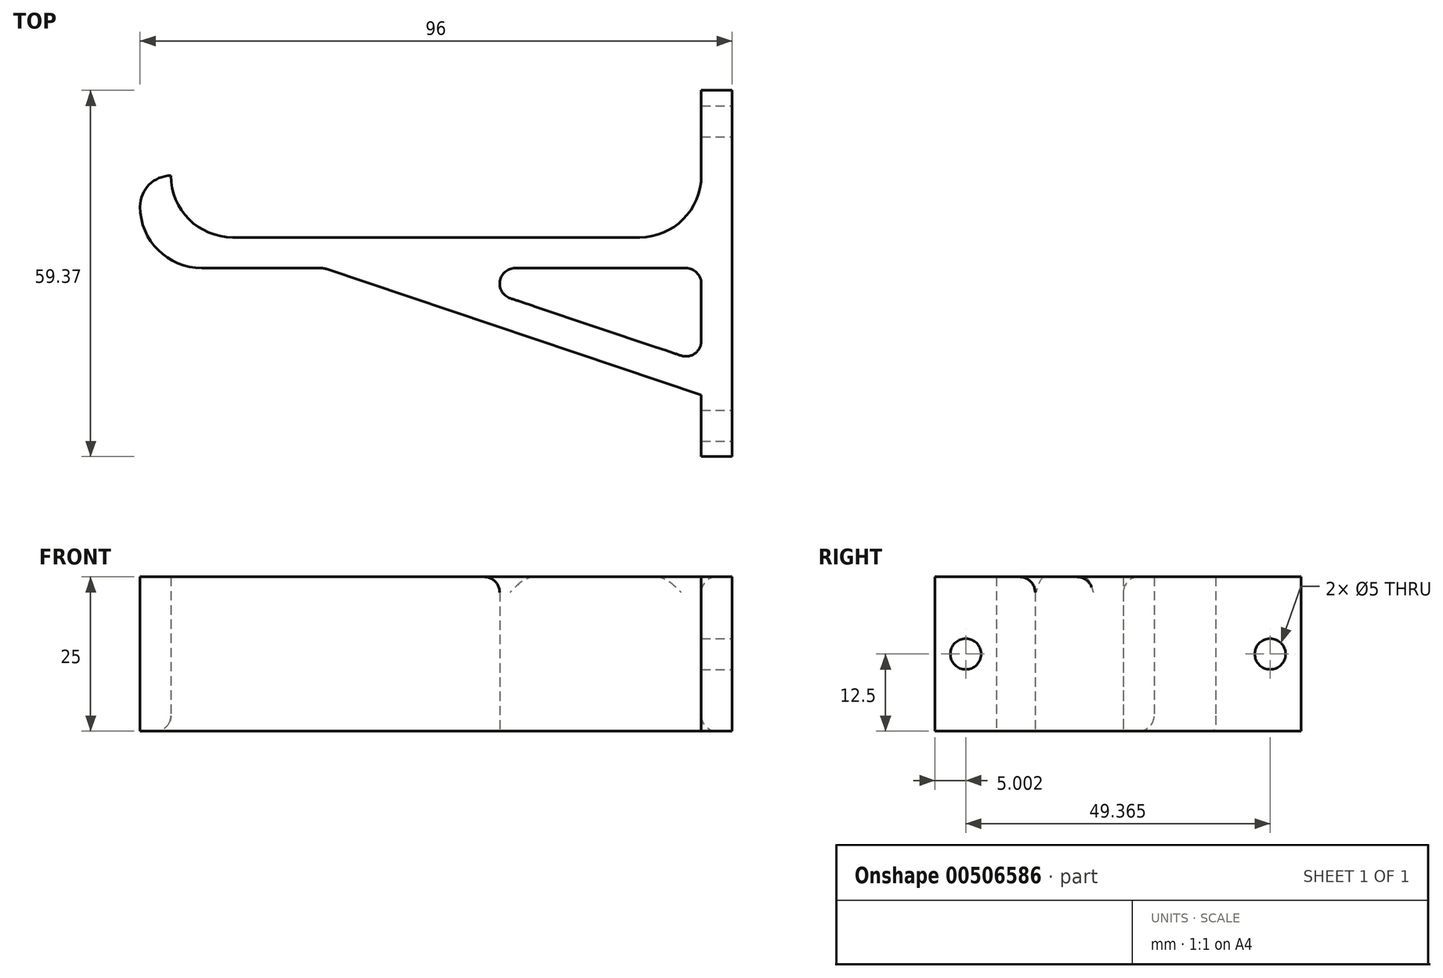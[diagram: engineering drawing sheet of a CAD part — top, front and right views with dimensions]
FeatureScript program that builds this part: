
annotation { "Feature Type Name" : "Feature", "Feature Type Description" : "" }
export const myFeature = defineFeature(function(context is Context, id is Id, definition is map)
    precondition{}
    {
        {
            var Q0;
            Q0=qCreatedBy(makeId("Top.planeOp"),FACE);
            var sketch = newSketch(context, id + "F0", { "sketchPlane" : qUnion([Q0])});
            skLineSegment(sketch, "E0", {"start": v(11.9, 15) * mm, "end": v(11.9, 15) * mm});
            skLineSegment(sketch, "E1", {"start": v(1.9, 5) * mm, "end": v(-64.1, 5) * mm});
            skLineSegment(sketch, "E2", {"start": v(-74.1, 15) * mm, "end": v(-74.1, 15) * mm});
            skLineSegment(sketch, "E3", {"start": v(-74.1, 15) * mm, "end": v(-79.1, 15) * mm});
            skLineSegment(sketch, "E4", {"start": v(-79.1, 15) * mm, "end": v(-79.1, 10) * mm});
            skLineSegment(sketch, "E5", {"start": v(-69.1, 0) * mm, "end": v(-49.3, 0) * mm});
            skLineSegment(sketch, "E6", {"start": v(11.9, 0) * mm, "end": v(11.9, -15.27) * mm});
            skLineSegment(sketch, "E7", {"start": v(11.9, -30.55) * mm, "end": v(16.9, -30.55) * mm});
            skLineSegment(sketch, "E8", {"start": v(16.9, -30.55) * mm, "end": v(16.9, 15) * mm});
            skLineSegment(sketch, "E9", {"start": v(-33.6, 0) * mm, "end": v(11.9, -15.27) * mm});
            skLineSegment(sketch, "E10", {"start": v(-49.3, 0) * mm, "end": v(11.9, -20.55) * mm});
            skLineSegment(sketch, "E11.trimOffspring", {"start": v(-33.6, 0) * mm, "end": v(11.9, 0) * mm});
            skLineSegment(sketch, "E12.trimOffspring", {"start": v(11.9, -20.55) * mm, "end": v(11.9, -30.55) * mm});
            skPoint(sketch, "E13.visualSharp", {"position": v(11.9, 5) * mm});
            skArc(sketch, "E13.filletArc", {"start": v(1.9, 5) * mm, "mid": v(8.97, 7.93) * mm, "end": v(11.9, 15) * mm});
            skPoint(sketch, "E14.visualSharp", {"position": v(-74.1, 5) * mm});
            skArc(sketch, "E14.filletArc", {"start": v(-74.1, 15) * mm, "mid": v(-71.17, 7.93) * mm, "end": v(-64.1, 5) * mm});
            skPoint(sketch, "E15.visualSharp", {"position": v(-79.1, 0) * mm});
            skArc(sketch, "E15.filletArc", {"start": v(-79.1, 10) * mm, "mid": v(-76.17, 2.93) * mm, "end": v(-69.1, 0) * mm});
            skLineSegment(sketch, "E16.right", {"start": v(16.9, 15) * mm, "end": v(16.9, 15) * mm});
            skLineSegment(sketch, "E17.top", {"start": v(11.9, 28.82) * mm, "end": v(16.9, 28.82) * mm});
            skLineSegment(sketch, "E17.left", {"start": v(11.9, 15) * mm, "end": v(11.9, 28.82) * mm});
            skLineSegment(sketch, "E17.right", {"start": v(16.9, 15) * mm, "end": v(16.9, 28.82) * mm});
            skSolve(sketch);
        }
        {
            var Q0;
            Q0=makeQuery(id+"F0.imprint","IMPRINT",FACE,{"disambiguationData":[TD([[makeQuery(id+"F0.imprint","IMPRINT",EDGE,{"derivedFrom":sQuery(id+"F0.wireOp",EDGE,"E1")}),1.0]])]});
            var Q1;
            Q1 = qSketchRegion(id + "F2", true);
            extrude(context, id + "F1", {"entities" : qUnion([Q0, Q1]), "depth" : 25 * mm});
        }
        {
            var Q0;
            Q0=makeQuery(id+"F1.opExtrude","SWEPT_FACE",FACE,{"disambiguationData":[OSD([sQuery(id+"F0.wireOp",EDGE,"E8"),sQuery(id+"F0.wireOp",EDGE,"E17.right")])]});
            var sketch = newSketch(context, id + "F2", { "sketchPlane" : qUnion([Q0])});
            skCircle(sketch, "E18", {"center": v(-25.55, 12.5) * mm, "radius": 2.5 * mm});
            skCircle(sketch, "E19", {"center": v(23.82, 12.5) * mm, "radius": 2.5 * mm});
            skSolve(sketch);
        }
        {
            var Q0;
            Q0=qSketchRegion(id+"F2",true);
            extrude(context, id + "F3", {"entities" : qUnion([Q0]), "operationType" : NewBodyOperationType.REMOVE, "oppositeDirection" : true, "depth" : 25 * mm});
        }
        {
            var Q0;
            Q0=makeQuery(id+"F1.opExtrude","SWEPT_EDGE",EDGE,{"disambiguationData":[OSD([sQuery(id+"F0.wireOp",EDGE,"E3"),sQuery(id+"F0.wireOp",EDGE,"E4")])]});
            fillet(context, id + "F4", {"entities" : qUnion([Q0]), "radius" : 5 * mm, "tangentPropagation" : true, "allowEdgeOverflow" : false});
        }
        {
            var Q0;
            Q0=makeQuery(id+"F1.opExtrude","SWEPT_EDGE",EDGE,{"disambiguationData":[OSD([sQuery(id+"F0.wireOp",EDGE,"E9"),sQuery(id+"F0.wireOp",EDGE,"E11.trimOffspring")])]});
            var Q1;
            Q1=makeQuery(id+"F1.opExtrude","SWEPT_EDGE",EDGE,{"disambiguationData":[OSD([sQuery(id+"F0.wireOp",EDGE,"E6"),sQuery(id+"F0.wireOp",EDGE,"E11.trimOffspring")])]});
            var Q2;
            Q2=makeQuery(id+"F1.opExtrude","SWEPT_EDGE",EDGE,{"disambiguationData":[OSD([sQuery(id+"F0.wireOp",EDGE,"E6"),sQuery(id+"F0.wireOp",EDGE,"E9")])]});
            var Q3;
            Q3=makeQuery(id+"F1.opExtrude","SWEPT_EDGE",EDGE,{"disambiguationData":[OSD([sQuery(id+"F0.wireOp",EDGE,"E5"),sQuery(id+"F0.wireOp",EDGE,"E10")])]});
            var Q4;
            Q4=makeQuery(id+"F1.opExtrude","CAP_EDGE",EDGE,{"disambiguationData":[OSD([sQuery(id+"F0.wireOp",EDGE,"E13.filletArc")])],"isStart":true});
            var Q5;
            Q5=makeQuery(id+"F1.opExtrude","CAP_EDGE",EDGE,{"disambiguationData":[OSD([sQuery(id+"F0.wireOp",EDGE,"E6")])],"isStart":false});
            var Q6;
            Q6=makeQuery(id+"F1.opExtrude","CAP_EDGE",EDGE,{"disambiguationData":[OSD([sQuery(id+"F0.wireOp",EDGE,"E11.trimOffspring")])],"isStart":false});
            fillet(context, id + "F5", {"entities" : qUnion([Q0, Q1, Q2, Q3, Q4, Q5, Q6]), "radius" : 2.5 * mm, "tangentPropagation" : true, "allowEdgeOverflow" : false});
        }
    });
